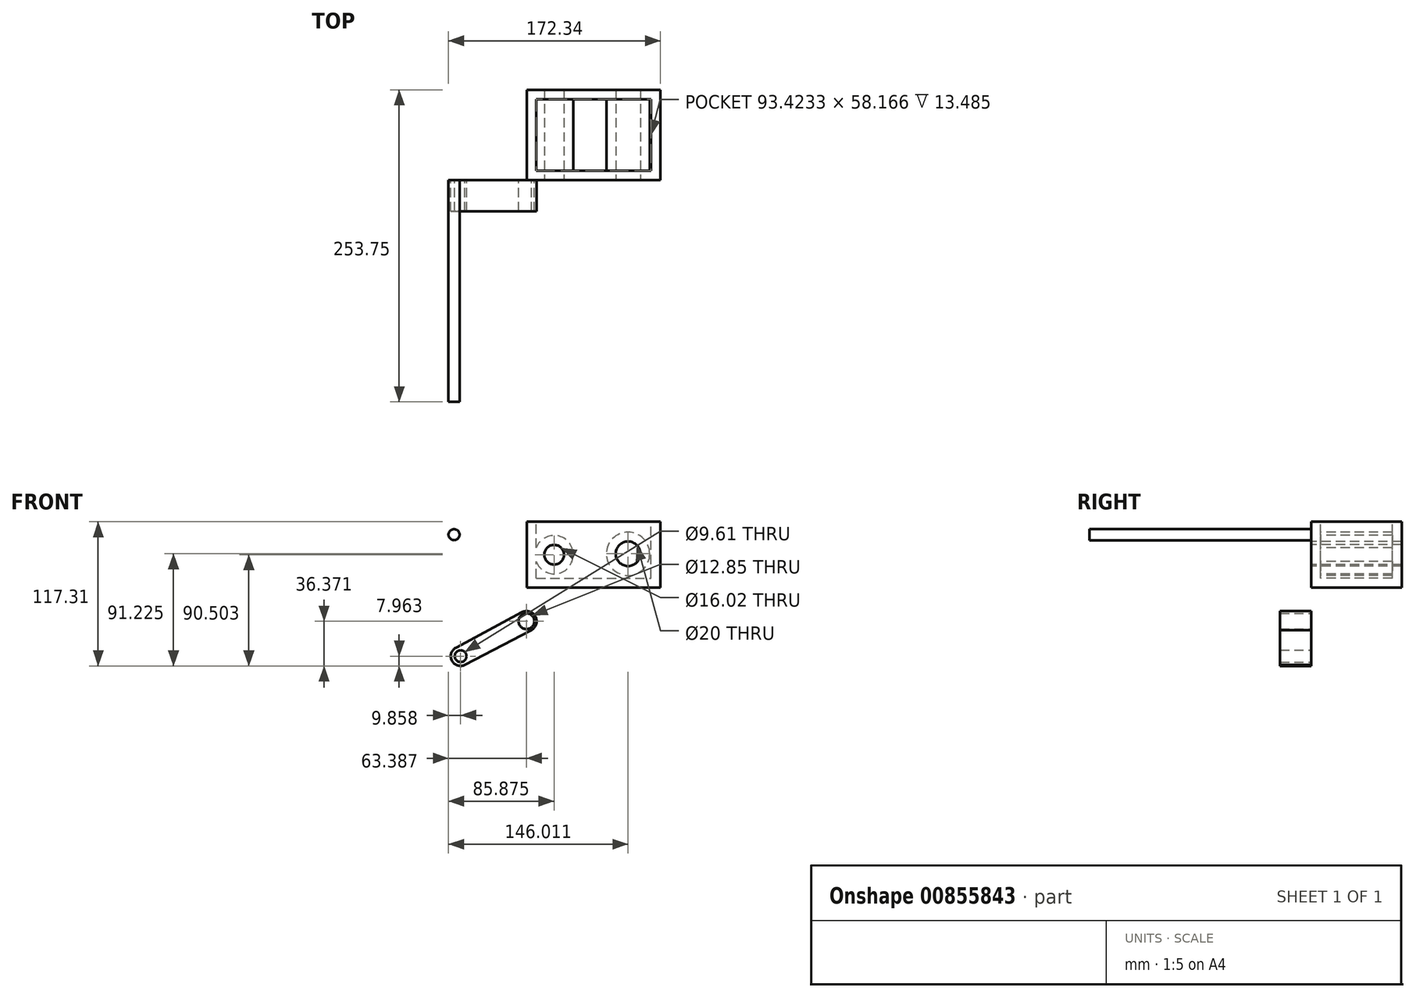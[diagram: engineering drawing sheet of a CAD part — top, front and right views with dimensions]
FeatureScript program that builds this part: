
annotation { "Feature Type Name" : "Feature", "Feature Type Description" : "" }
export const myFeature = defineFeature(function(context is Context, id is Id, definition is map)
    precondition{}
    {
        {
            var Q0;
            Q0=qCreatedBy(makeId("Front.planeOp"),FACE);
            var sketch = newSketch(context, id + "F0", { "sketchPlane" : qUnion([Q0])});
            skLineSegment(sketch, "E0.bottom", {"start": v(0, 0) * mm, "end": v(108.66, 0) * mm});
            skLineSegment(sketch, "E0.top", {"start": v(0, 53.56) * mm, "end": v(108.66, 53.56) * mm});
            skLineSegment(sketch, "E0.left", {"start": v(0, 0) * mm, "end": v(0, 53.56) * mm});
            skLineSegment(sketch, "E0.right", {"start": v(108.66, 0) * mm, "end": v(108.66, 53.56) * mm});
            skCircle(sketch, "E1", {"center": v(22.2, 26.75) * mm, "radius": 8.01 * mm});
            skCircle(sketch, "E2", {"center": v(82.33, 27.47) * mm, "radius": 10 * mm});
            skSolve(sketch);
        }
        {
            var Q0;
            Q0=makeQuery(id+"F0.imprint","IMPRINT",FACE,{"disambiguationData":[TD([[makeQuery(id+"F0.imprint","IMPRINT",EDGE,{"derivedFrom":sQuery(id+"F0.wireOp",EDGE,"E0.bottom")}),1.0]])]});
            extrude(context, id + "F1", {"entities" : qUnion([Q0]), "oppositeDirection" : true, "depth" : 73.4 * mm, "offsetDistance" : 25.4 * mm});
        }
        {
            var Q0;
            Q0=makeQuery(id+"F1.opExtrude","SWEPT_FACE",FACE,{"disambiguationData":[OSD([sQuery(id+"F0.wireOp",EDGE,"E0.top")])]});
            shell(context, id + "F2", {"entities" : qUnion([Q0]), "thickness" : 7.62 * mm});
        }
        {
            var Q0;
            Q0=qCreatedBy(makeId("Front.planeOp"),FACE);
            var sketch = newSketch(context, id + "F3", { "sketchPlane" : qUnion([Q0])});
            skCircle(sketch, "E3", {"center": v(-59.19, 43.03) * mm, "radius": 4.49 * mm});
            skSolve(sketch);
        }
        {
            var Q0;
            Q0=makeQuery(id+"F3.imprint","IMPRINT",FACE,{"disambiguationData":[TD([[makeQuery(id+"F3.imprint","IMPRINT",EDGE,{"derivedFrom":sQuery(id+"F3.wireOp",EDGE,"E3")}),1.0]])]});
            extrude(context, id + "F4", {"entities" : qUnion([Q0]), "depth" : 180.34 * mm, "offsetDistance" : 25.4 * mm});
        }
        {
            var Q0;
            Q0=qCreatedBy(makeId("Front.planeOp"),FACE);
            var sketch = newSketch(context, id + "F5", { "sketchPlane" : qUnion([Q0])});
            skLineSegment(sketch, "E4", {"start": v(-57.59, -48.77) * mm, "end": v(-4.2, -20.1) * mm});
            skArc(sketch, "E5", {"start": v(3.7, -34.6) * mm, "mid": v(6.96, -23.42) * mm, "end": v(-4.2, -20.1) * mm});
            skArc(sketch, "E6", {"start": v(-57.59, -48.77) * mm, "mid": v(-60.9, -59.41) * mm, "end": v(-50.34, -62.94) * mm});
            skLineSegment(sketch, "E7", {"start": v(-50.34, -62.94) * mm, "end": v(3.7, -34.6) * mm});
            skCircle(sketch, "E8", {"center": v(-53.82, -55.79) * mm, "radius": 4.8 * mm});
            skCircle(sketch, "E9", {"center": v(-0.3, -27.38) * mm, "radius": 6.42 * mm});
            skSolve(sketch);
        }
        {
            var Q0;
            Q0=makeQuery(id+"F5.imprint","IMPRINT",FACE,{"disambiguationData":[TD([[makeQuery(id+"F5.imprint","IMPRINT",EDGE,{"derivedFrom":sQuery(id+"F5.wireOp",EDGE,"E4")}),-1.0]])]});
            extrude(context, id + "F6", {"entities" : qUnion([Q0]), "depth" : 25.4 * mm, "offsetDistance" : 25.4 * mm});
        }
    });
